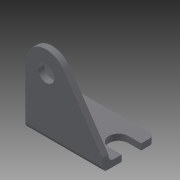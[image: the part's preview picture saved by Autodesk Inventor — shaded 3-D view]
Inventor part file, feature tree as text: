
AUTODESK INVENTOR PART (.ipt)
format: ipt  version: 2014 (Build 180170000, 170)  size: 151,552 bytes
history: native  units: in
note: dims shown in document units (in); Inventor stores cm internally (conversion verified against a paired STEP export)
features: other x28, sketch x8, extrude x5, hole x3
ambient origin geometry x8: Origin, YZ Plane, XZ Plane, XY Plane, X Axis, Y Axis, Z Axis, Center Point
bodies: Solid1 (feature_tree)
feature tree (44):
  extrude  "Extrusion1"  Depth=0.51in TaperAngle=0.0deg
  extrude  "Extrusion2"  Depth=0.0598in TaperAngle=0.0deg
  hole  "Hole1"  [1 undecoded]
  hole  "Hole2"  [1 undecoded]
  hole  "Hole3"  [1 undecoded]
  sketch  "Sketch_6"
  sketch  "Sketch_7"
  extrude  "Extrusion3"  [1 undecoded]
  extrude  "Extrusion4"  [1 undecoded]
  extrude  "Extrusion5"  [1 undecoded]
  other  "c2_XY"
  other  "c2_YZ"
  other  "c2_ZX"
  other  "c2_X"
  other  "c2_Y"
  other  "c2_Z"
  other  "c2_Center"
  other  "k2_XY"
  other  "k2_YZ"
  other  "k2_ZX"
  other  "k2_X"
  other  "k2_Y"
  other  "k2_Z"
  other  "k2_Center"
  other  "to_dummy_R_XY"
  other  "to_dummy_R_YZ"
  other  "to_dummy_R_ZX"
  other  "to_dummy_R_X"
  other  "to_dummy_R_Y"
  other  "to_dummy_R_Z"
  other  "to_dummy_R_Center"
  other  "to_pin_R_XY"
  other  "to_pin_R_YZ"
  other  "to_pin_R_ZX"
  other  "to_pin_R_X"
  other  "to_pin_R_Y"
  other  "to_pin_R_Z"
  other  "to_pin_R_Center"
  sketch  "Sketch_1"  dims[d0=0.75in d1=0.0in d2=0.51in d3=0.0in]
  sketch  "Sketch_2"  dims[d4=0.1585in d5=0.75in d6=0.375in d7=0.25in d8=0.5635in d9=0.0598in d10=0.0in]
  sketch  "Sketch3"  dims[d11=0.19in d12=0.75in d13=0.375in d14=0.25in d15=0.5635in d16=0.0598in d17=0.0in]
  sketch  "Sketch4"  dims[d18=0.19in d19=0.75in d20=0.375in d21=0.25in d22=0.5635in d23=0.0598in d24=0.0in d25=0.0598in d26=0.0in]
  sketch  "Sketch5"  dims[d27=0.0598in d28=0.0in d29=0.0598in d30=0.0in]
  sketch  "Sketch_8"
note: 6 required parameter values undecoded (feature->parameter linkage not recoverable at this tier; creation-order binding heuristic only, values carry confidence <= 0.55)
